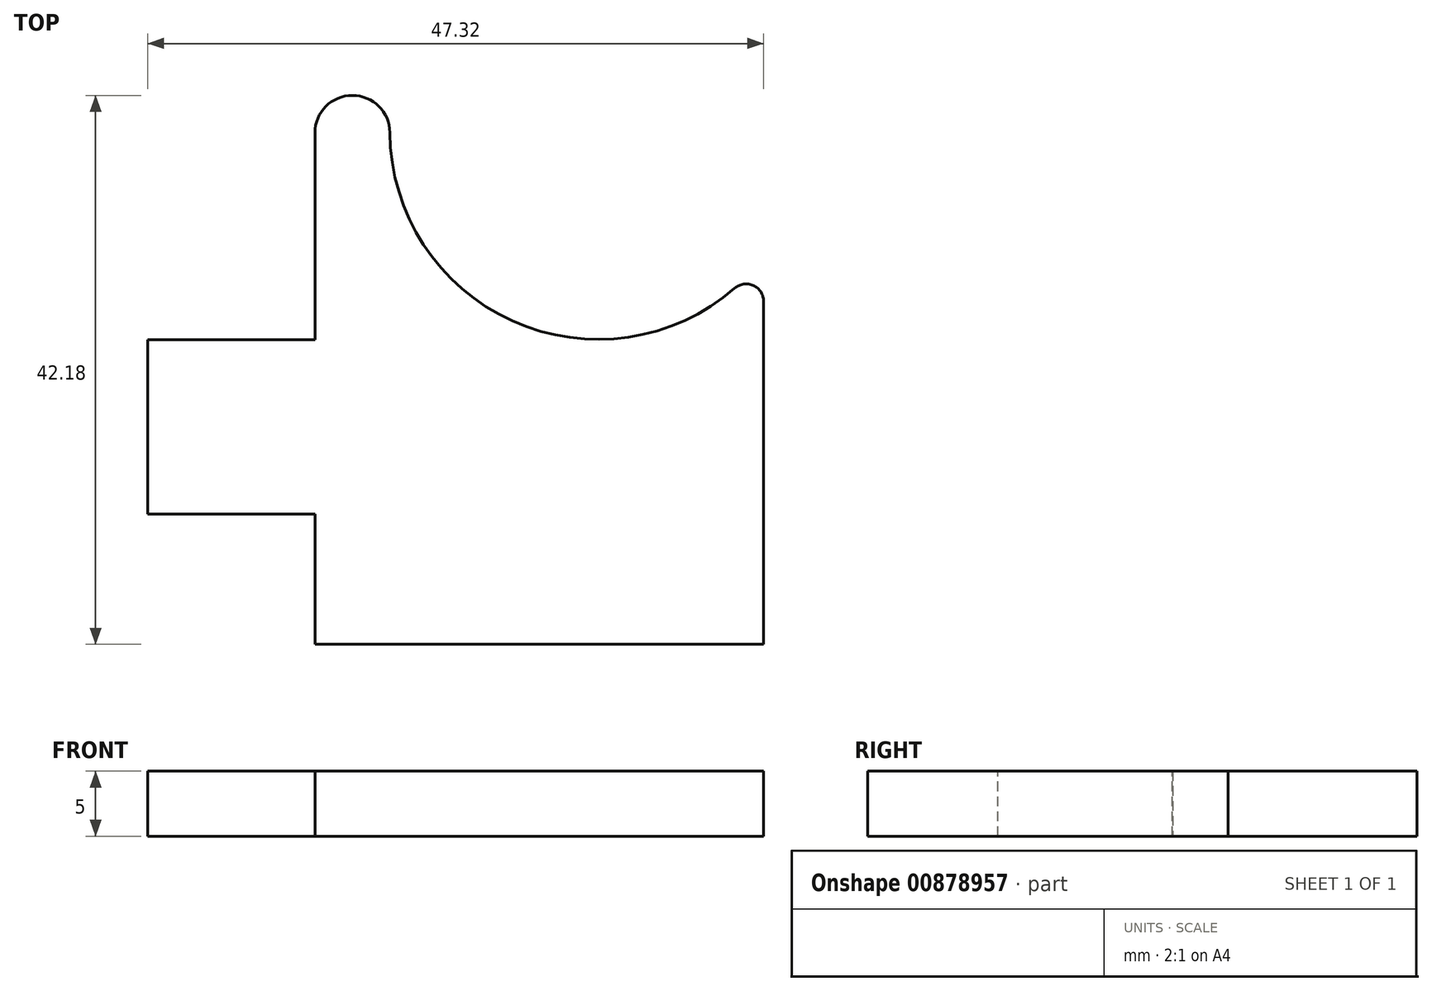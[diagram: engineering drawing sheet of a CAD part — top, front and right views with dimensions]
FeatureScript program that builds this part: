
annotation { "Feature Type Name" : "Feature", "Feature Type Description" : "" }
export const myFeature = defineFeature(function(context is Context, id is Id, definition is map)
    precondition{}
    {
        {
            var Q0;
            Q0=qCreatedBy(makeId("Top.planeOp"),FACE);
            var sketch = newSketch(context, id + "F0", { "sketchPlane" : qUnion([Q0])});
            skLineSegment(sketch, "E0.bottom", {"start": v(0, 0) * mm, "end": v(34.47, 0) * mm});
            skLineSegment(sketch, "E0.left", {"start": v(0, 0) * mm, "end": v(0, 29.3) * mm});
            skLineSegment(sketch, "E0.right", {"start": v(34.47, 0) * mm, "end": v(34.47, 16.35) * mm});
            skArc(sketch, "E1", {"start": v(5.76, 29.32) * mm, "mid": v(15.17, 14.85) * mm, "end": v(32.26, 17.36) * mm});
            skCircle(sketch, "E2", {"center": v(33.13, 16.35) * mm, "radius": 1.34 * mm});
            skCircle(sketch, "E3", {"center": v(2.88, 29.3) * mm, "radius": 2.88 * mm});
            skSolve(sketch);
        }
        {
            var Q0;
            Q0=qSketchRegion(id+"F0",true);
            extrude(context, id + "F1", {"entities" : qUnion([Q0]), "depth" : 5 * mm, "offsetDistance" : 25 * mm});
        }
        {
            var Q0;
            Q0=makeQuery(id+"F1.opExtrude","CAP_FACE",FACE,{"disambiguationData":[OSD([sQuery(id+"F0.wireOp",EDGE,"E0.bottom"),sQuery(id+"F0.wireOp",EDGE,"E0.left"),sQuery(id+"F0.wireOp",EDGE,"E0.right"),sQuery(id+"F0.wireOp",EDGE,"E1"),sQuery(id+"F0.wireOp",EDGE,"E2"),sQuery(id+"F0.wireOp",EDGE,"E3")])],"isStart":false});
            var sketch = newSketch(context, id + "F2", { "sketchPlane" : qUnion([Q0])});
            skLineSegment(sketch, "E4", {"start": v(34.47, 0) * mm, "end": v(34.47, -10) * mm});
            skLineSegment(sketch, "E5", {"start": v(34.47, -10) * mm, "end": v(0, -10) * mm});
            skLineSegment(sketch, "E6", {"start": v(0, -10) * mm, "end": v(0, 0) * mm});
            skLineSegment(sketch, "E7", {"start": v(0, 25.49) * mm, "end": v(-110.38, 52.94) * mm});
            skLineSegment(sketch, "E8", {"start": v(0, 0) * mm, "end": v(-12.85, 0) * mm});
            skLineSegment(sketch, "E9", {"start": v(-12.85, 0) * mm, "end": v(-12.85, 13.4) * mm});
            skLineSegment(sketch, "E10", {"start": v(-12.85, 13.4) * mm, "end": v(0, 13.4) * mm});
            skLineSegment(sketch, "E11", {"start": v(0, 13.4) * mm, "end": v(0, 0) * mm});
            skSolve(sketch);
        }
        {
            var Q0;
            {var subQ0=makeQuery(id+"F1.opExtrude","CAP_EDGE",EDGE,{"disambiguationData":[OSD([sQuery(id+"F0.wireOp",EDGE,"E0.bottom")])],"isStart":false});Q0=makeQuery(id+"F2.imprint","IMPRINT",FACE,{"disambiguationData":[TD([[makeQuery(id+"F2.imprint","IMPRINT",EDGE,{"derivedFrom":subQ0}),1.0]])]});}
            var Q1;
            Q1=makeQuery(id+"F2.imprint","IMPRINT",FACE,{"disambiguationData":[TD([[makeQuery(id+"F2.imprint","IMPRINT",EDGE,{"derivedFrom":sQuery(id+"F2.wireOp",EDGE,"E4")}),-1.0]])]});
            var Q2;
            {var subQ0=sQuery(id+"F2.wireOp",EDGE,"irv26uyZ-Q05m-Obbf-i6gP-vnwM5PRfqptf");Q2=makeQuery(id+"F2.imprint","IMPRINT",FACE,{"disambiguationData":[TD([[makeQuery(id+"F2.imprint","IMPRINT",EDGE,{"derivedFrom":subQ0}),-1.0]])]});}
            var Q3;
            Q3=makeQuery(id+"F2.imprint","IMPRINT",FACE,{"disambiguationData":[TD([[makeQuery(id+"F2.imprint","IMPRINT",EDGE,{"derivedFrom":sQuery(id+"F2.wireOp",EDGE,"E6")}),1.0]])]});
            var Q4;
            Q4=makeQuery(id+"F2.imprint","IMPRINT",FACE,{"disambiguationData":[TD([[makeQuery(id+"F2.imprint","IMPRINT",EDGE,{"derivedFrom":sQuery(id+"F2.wireOp",EDGE,"E8")}),-1.0]])]});
            extrude(context, id + "F3", {"entities" : qUnion([Q0, Q1, Q2, Q3, Q4]), "operationType" : NewBodyOperationType.ADD, "oppositeDirection" : true, "depth" : 5 * mm, "offsetDistance" : 25 * mm});
        }
    });
